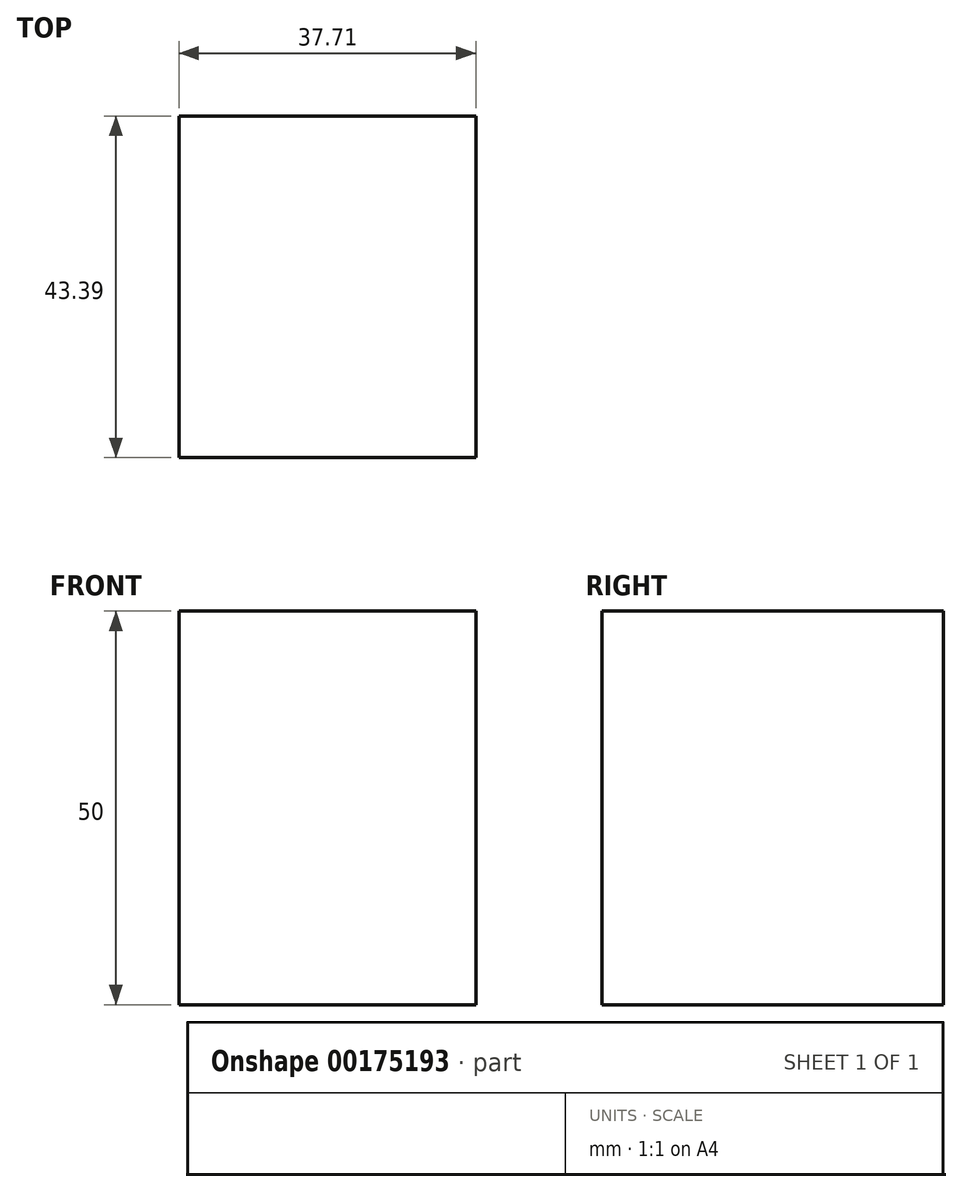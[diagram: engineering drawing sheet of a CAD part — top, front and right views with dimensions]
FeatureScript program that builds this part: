
annotation { "Feature Type Name" : "Feature", "Feature Type Description" : "" }
export const myFeature = defineFeature(function(context is Context, id is Id, definition is map)
    precondition{}
    {
        {
            var Q0;
            Q0=qCreatedBy(makeId("Top.planeOp"),FACE);
            var sketch = newSketch(context, id + "F0", { "sketchPlane" : qUnion([Q0])});
            skLineSegment(sketch, "E0.bottom", {"start": v(0, 0) * mm, "end": v(37.71, 0) * mm});
            skLineSegment(sketch, "E0.top", {"start": v(0, 43.4) * mm, "end": v(37.71, 43.4) * mm});
            skLineSegment(sketch, "E0.left", {"start": v(0, 0) * mm, "end": v(0, 43.4) * mm});
            skLineSegment(sketch, "E0.right", {"start": v(37.71, 0) * mm, "end": v(37.71, 43.4) * mm});
            skSolve(sketch);
        }
        {
            var Q0;
            Q0 = qSketchRegion(id + "F0", true);
            extrude(context, id + "F1", {"entities" : qUnion([Q0]), "depth" : 50 * mm});
        }
    });
